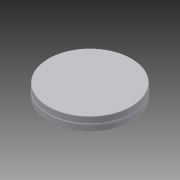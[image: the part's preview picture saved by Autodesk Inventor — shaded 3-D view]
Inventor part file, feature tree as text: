
AUTODESK INVENTOR PART (.ipt)
format: ipt  version: 2014 (Build 180170000, 170)  size: 121,856 bytes
history: native  units: in
note: dims shown in document units (in); Inventor stores cm internally (conversion verified against a paired STEP export)
features: revolve x1, sketch x1, reference x1
ambient origin geometry x8: Origin, YZ Plane, XZ Plane, XY Plane, X Axis, Y Axis, Z Axis, Center Point
bodies: Solid1 (feature_tree)
feature tree (3):
  revolve  "Revolution1"  [1 undecoded]
  sketch  "Sketch1"  dims[d1=0.005in d3=0.005in d4=90.0deg]
  reference  "Reference1"
note: 1 required parameter value undecoded (feature->parameter linkage not recoverable at this tier; creation-order binding heuristic only, values carry confidence <= 0.55)
